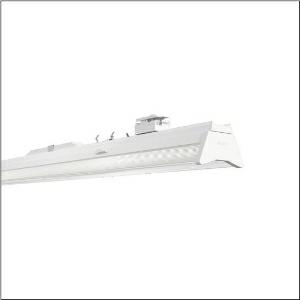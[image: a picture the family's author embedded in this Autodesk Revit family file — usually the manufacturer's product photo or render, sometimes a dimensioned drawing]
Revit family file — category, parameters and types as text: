
# Revit family: licross_r__21_performance_mo_52td16mn4a5g_2767
name_source: partatom
category: Lighting Fixtures
units: mm (PartAtom-declared; Revit-internal decimal feet)

## family parameters
Cut with Voids When Loaded = No
Host = Face
Light Source = No
Part Type = Normal
Room Calculation Point = No
Round Connector Dimension = Use Diameter
Shared = No

## types (1)
- --- (1 x LED, 10890 lm, 60.5 W, 4000K)
    Apparent Load = 61 VA
    CIE Flux Codes = 66 88 96 79 100
    Color Rendering = 80
    Color Temperature = 4000K
    Default Elevation = 1800 mm
    Description = Licross® 21 Performance MO, luminaire insert, of sheet steel, galvanised, coil coated, white, length: 1.500mm, width: 120mm, height: 123mm, LED rated luminous flux: 10.890lm, light colour: 840, control gear: ON/OFF Multilumen, with plug, 3-pole, with phase selection, mains connection: 220..240V, AC, 50/60Hz, rated input power: 61W, halogen-free wiring, primary light control with lens, of plastic, primary optical cover: cover, of PMMA, light emission: direct/indirect distribution, primary light characteristic: symmetric, protection rating (complete): IP54, insulation class (complete): insulation class I (protective earthing), certification: CE, ENEC, UKCA, protection symbol: D if used in an environment with non-conductive dust loads with corresponding accessories, impact resistance: IK06, permissible ambient temperature for indoor applications: -35..+45°C, corresponds to IFS (International Featured Standards) requirements for safety and quality in the food industry, reducing of maximum allowable ambient temperature of 5°C with ceiling mounting, LABS conformity tested according to VDMA 24364:2018-05, packaging unit: 1 piece
    Height = 114 mm
    Lamp = 1 x LED
    Lamp Light Flux = 10890 lm
    Lamp Power = 60.5 W
    Lamp count = 1
    Length = 1500 mm
    Luminous efficacy = 180 lm/W
    Manufacturer = Siteco
    ModVariant = No
    Model = 52TD16MN4A5G
    Mounting Place = Ceiling
    Mounting Type = Pendant
    Number of Poles = 1
    OnlyDefault = Yes
    Power Factor = 1
    Product Name = Licross® 21 Performance MO
    Product group = luminaire insert
    ProductGroupID = 902
    Protection Class = Protection class I
    Protection Degree = IP 54
    RLX_Detail_Level = 1
    RLX_Emergency_Light_Flux = 0 lm
    RLX_Emergency_Type = 0
    RLX_Emergency_Type_DB = No
    RlxData = <blob elided: 31841 chars, md5=be7b402d>
    Socket = socket
    Standby Power = 0 W
    System Light Flux = 10890 lm
    System Power = 61 W
    Type Comments = factory setting: luminous flux: 100 % | (A | C | E) | 140 mA
    Type Image = l_1256138.jpg
    URL = http://relux.com
    VarID = @adj_109224
    Voltage = 0 V
    Weight = 0.00 kg
    Width = 120 mm

## geometry (parser evidence)
native form markers: Blend x4, Sweep x12
no freeform markers — native parametric forms only
